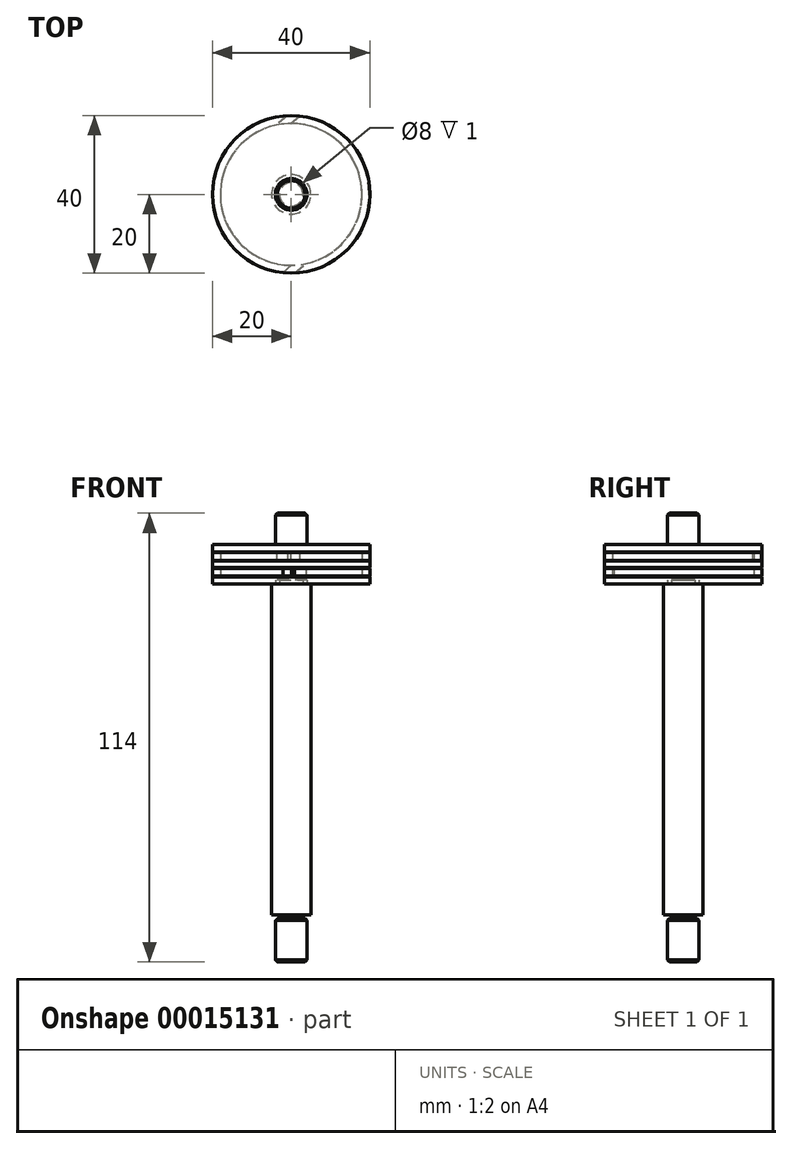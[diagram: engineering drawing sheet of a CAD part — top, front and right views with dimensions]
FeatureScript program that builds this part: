
annotation { "Feature Type Name" : "Feature", "Feature Type Description" : "" }
export const myFeature = defineFeature(function(context is Context, id is Id, definition is map)
    precondition{}
    {
        {
            var Q0;
            Q0=qCreatedBy(makeId("Front.planeOp"),FACE);
            var sketch = newSketch(context, id + "F0", { "sketchPlane" : qUnion([Q0])});
            skLineSegment(sketch, "E0", {"start": v(0, 0) * mm, "end": v(0, 13.15) * mm, "construction": true});
            skLineSegment(sketch, "E1", {"start": v(0, 0) * mm, "end": v(20, 0) * mm});
            skLineSegment(sketch, "E2", {"start": v(20, 0) * mm, "end": v(20, 2) * mm});
            skLineSegment(sketch, "E3", {"start": v(20, 2) * mm, "end": v(18, 2) * mm});
            skLineSegment(sketch, "E4", {"start": v(18, 2) * mm, "end": v(18, 4) * mm});
            skLineSegment(sketch, "E5", {"start": v(18, 4) * mm, "end": v(20, 4) * mm});
            skLineSegment(sketch, "E6", {"start": v(20, 4) * mm, "end": v(20, 6) * mm});
            skLineSegment(sketch, "E7", {"start": v(20, 6) * mm, "end": v(18, 6) * mm});
            skLineSegment(sketch, "E8", {"start": v(18, 6) * mm, "end": v(18, 8) * mm});
            skLineSegment(sketch, "E9", {"start": v(18, 8) * mm, "end": v(20, 8) * mm});
            skLineSegment(sketch, "E10", {"start": v(20, 8) * mm, "end": v(20, 10) * mm});
            skLineSegment(sketch, "E11", {"start": v(20, 10) * mm, "end": v(0, 10) * mm});
            skLineSegment(sketch, "E12", {"start": v(0, 10) * mm, "end": v(0, 0) * mm});
            skLineSegment(sketch, "E13", {"start": v(18, 10) * mm, "end": v(18, 0) * mm, "construction": true});
            skLineSegment(sketch, "E14", {"start": v(20, 10) * mm, "end": v(20, 0) * mm, "construction": true});
            skLineSegment(sketch, "E15.0.MirrorCS", {"start": v(-20, 10) * mm, "end": v(0, 10) * mm});
            skLineSegment(sketch, "E16.0.MirrorCS", {"start": v(0, 0) * mm, "end": v(-20, 0) * mm});
            skLineSegment(sketch, "E17.0.MirrorCS", {"start": v(-18, 2) * mm, "end": v(-18, 4) * mm});
            skLineSegment(sketch, "E18.0.MirrorCS", {"start": v(-18, 6) * mm, "end": v(-18, 8) * mm});
            skLineSegment(sketch, "E19.0.MirrorCS", {"start": v(-18, 8) * mm, "end": v(-20, 8) * mm});
            skLineSegment(sketch, "E20.0.MirrorCS", {"start": v(-20, 6) * mm, "end": v(-18, 6) * mm});
            skLineSegment(sketch, "E21.0.MirrorCS", {"start": v(-18, 4) * mm, "end": v(-20, 4) * mm});
            skLineSegment(sketch, "E22.0.MirrorCS", {"start": v(-20, 2) * mm, "end": v(-18, 2) * mm});
            skLineSegment(sketch, "E23.0.MirrorCS", {"start": v(-20, 0) * mm, "end": v(-20, 2) * mm});
            skLineSegment(sketch, "E24.0.MirrorCS", {"start": v(-20, 4) * mm, "end": v(-20, 6) * mm});
            skLineSegment(sketch, "E25.0.MirrorCS", {"start": v(-20, 8) * mm, "end": v(-20, 10) * mm});
            skLineSegment(sketch, "E26", {"start": v(4, 0) * mm, "end": v(4, 10) * mm});
            skLineSegment(sketch, "E27.0.MirrorCS", {"start": v(-4, 0) * mm, "end": v(-4, 10) * mm});
            skSolve(sketch);
        }
        {
            var Q0;
            {var subQ3=sQuery(id+"F0.wireOp",EDGE,"E2");Q0=makeQuery(id+"F0.imprint","IMPRINT",FACE,{"disambiguationData":[TD([[makeQuery(id+"F0.imprint","IMPRINT",EDGE,{"derivedFrom":subQ3}),1.0]])]});}
            var Q1;
            Q1=sQuery(id+"F0.wireOp",EDGE,"E0");
            revolve(context, id + "F1", {"entities" : qUnion([Q0]), "axis" : qUnion([Q1]), "revolveType" : RevolveType.FULL});
        }
        {
            var Q0;
            Q0=makeQuery(id+"F1.opRevolve","SWEPT_FACE",FACE,{"disambiguationData":[OSD([sQuery(id+"F0.wireOp",EDGE,"E3")])]});
            var sketch = newSketch(context, id + "F2", { "sketchPlane" : qUnion([Q0])});
            skArc(sketch, "E28.0", {"start": v(0.89, -19.98) * mm, "mid": v(0.63, 20) * mm, "end": v(-2.14, -19.89) * mm});
            skArc(sketch, "E29.0", {"start": v(3.75, -17.6) * mm, "mid": v(-1.96, 17.9) * mm, "end": v(0.14, -18) * mm});
            skLineSegment(sketch, "E30", {"start": v(0, 0) * mm, "end": v(0, -20) * mm, "construction": true});
            skLineSegment(sketch, "E31", {"start": v(0.14, -18) * mm, "end": v(-2.14, -19.89) * mm});
            skLineSegment(sketch, "E32", {"start": v(0.89, -19.98) * mm, "end": v(3.75, -17.6) * mm});
            skSolve(sketch);
        }
        {
            var Q0;
            Q0=makeQuery(id+"F2.imprint","IMPRINT",FACE,{"disambiguationData":[TD([[makeQuery(id+"F2.imprint","IMPRINT",EDGE,{"derivedFrom":sQuery(id+"F2.wireOp",EDGE,"E28.0")}),-1.0]])]});
            extrude(context, id + "F3", {"entities" : qUnion([Q0]), "depth" : 2 * mm});
        }
        {
            var Q0;
            Q0=makeQuery(id+"F1.opRevolve","SWEPT_EDGE",EDGE,{"disambiguationData":[OSD([sQuery(id+"F0.wireOp",EDGE,"E9"),sQuery(id+"F0.wireOp",EDGE,"E10")])]});
            var Q1;
            Q1=makeQuery(id+"F1.opRevolve","SWEPT_EDGE",EDGE,{"disambiguationData":[OSD([sQuery(id+"F0.wireOp",EDGE,"E6"),sQuery(id+"F0.wireOp",EDGE,"E7")])]});
            var Q2;
            Q2=makeQuery(id+"F1.opRevolve","SWEPT_EDGE",EDGE,{"disambiguationData":[OSD([sQuery(id+"F0.wireOp",EDGE,"E5"),sQuery(id+"F0.wireOp",EDGE,"E6")])]});
            var Q3;
            Q3=makeQuery(id+"F1.opRevolve","SWEPT_EDGE",EDGE,{"disambiguationData":[OSD([sQuery(id+"F0.wireOp",EDGE,"E2"),sQuery(id+"F0.wireOp",EDGE,"E3")])]});
            chamfer(context, id + "F4", {"entities" : qUnion([Q0, Q1, Q2, Q3]), "width" : .2 * mm, "tangentPropagation" : true});
        }
        {
            var Q0;
            Q0=makeQuery(id+"F3.opExtrude","SWEPT_BODY",BODY,{"disambiguationData":[OSD([sQuery(id+"F2.wireOp",EDGE,"E28.0"),sQuery(id+"F2.wireOp",EDGE,"E29.0"),sQuery(id+"F2.wireOp",EDGE,"E31"),sQuery(id+"F2.wireOp",EDGE,"E32")])]});
            var Q1;
            Q1=makeQuery(id+"F1.opRevolve","SWEPT_FACE",FACE,{"disambiguationData":[OSD([sQuery(id+"F0.wireOp",EDGE,"E26")])]});
            transform(context, id + "F5", {"entities" : qUnion([Q0]), "transformType" : TransformType.TRANSLATION_3D, "dx" : 0 * mm, "dy" : 0 * mm, "dz" : 4 * mm, "makeCopy" : true});
        }
        {
            var Q0;
            Q0=makeQuery(id+"F5.opPattern","COPY",BODY,{"derivedFrom":makeQuery(id+"F3.opExtrude","SWEPT_BODY",BODY,{"disambiguationData":[OSD([sQuery(id+"F2.wireOp",EDGE,"E28.0"),sQuery(id+"F2.wireOp",EDGE,"E29.0"),sQuery(id+"F2.wireOp",EDGE,"E31"),sQuery(id+"F2.wireOp",EDGE,"E32")])]}),"instanceName":"1"});
            var Q1;
            Q1=makeQuery(id+"F1.opRevolve","SWEPT_FACE",FACE,{"disambiguationData":[OSD([sQuery(id+"F0.wireOp",EDGE,"E26")])]});
            transform(context, id + "F6", {"entities" : qUnion([Q0]), "transformType" : TransformType.ROTATION, "transformAxis" : qUnion([Q1]), "angle" : 180 * degree, "makeCopy" : false});
        }
        {
            var Q0;
            Q0=makeQuery(id+"F1.opRevolve","SWEPT_FACE",FACE,{"disambiguationData":[OSD([sQuery(id+"F0.wireOp",EDGE,"E1")])]});
            var sketch = newSketch(context, id + "F7", { "sketchPlane" : qUnion([Q0])});
            skPoint(sketch, "E33.0", {"position": v(0, 0) * mm});
            skCircle(sketch, "E34", {"center": v(0, 0) * mm, "radius": 5 * mm});
            skCircle(sketch, "E35", {"center": v(0, 0) * mm, "radius": 3 * mm});
            skSolve(sketch);
        }
        {
            var Q0;
            Q0=makeQuery(id+"F7.imprint","IMPRINT",FACE,{"disambiguationData":[TD([[makeQuery(id+"F7.imprint","IMPRINT",EDGE,{"derivedFrom":sQuery(id+"F7.wireOp",EDGE,"E35")}),1.0]])]});
            var Q1;
            Q1=makeQuery(id+"F7.imprint","IMPRINT",FACE,{"disambiguationData":[TD([[makeQuery(id+"F7.imprint","IMPRINT",EDGE,{"derivedFrom":sQuery(id+"F7.wireOp",EDGE,"E35")}),-1.0]])]});
            var Q2;
            Q2=makeQuery(id+"F7.imprint","IMPRINT",FACE,{"disambiguationData":[TD([[makeQuery(id+"F7.imprint","IMPRINT",EDGE,{"derivedFrom":sQuery(id+"F7.wireOp",EDGE,"E34")}),1.0]])]});
            extrude(context, id + "F8", {"entities" : qUnion([Q0, Q1, Q2]), "depth" : (114 - 12 - 18) * mm});
        }
        {
            var Q0;
            Q0=makeQuery(id+"F7.imprint","IMPRINT",FACE,{"disambiguationData":[TD([[makeQuery(id+"F7.imprint","IMPRINT",EDGE,{"derivedFrom":sQuery(id+"F7.wireOp",EDGE,"E35")}),1.0]])]});
            extrude(context, id + "F9", {"entities" : qUnion([Q0]), "operationType" : NewBodyOperationType.ADD, "oppositeDirection" : true, "depth" : 1 * mm});
        }
        {
            var Q0;
            Q0=makeQuery(id+"F9.opExtrude","CAP_FACE",FACE,{"disambiguationData":[OSD([sQuery(id+"F7.wireOp",EDGE,"E35")])],"isStart":false});
            var sketch = newSketch(context, id + "F10", { "sketchPlane" : qUnion([Q0])});
            skCircle(sketch, "E36.0.0", {"center": v(0, 0) * mm, "radius": 5 * mm, "construction": true});
            skCircle(sketch, "E37.0.0", {"center": v(0, 0) * mm, "radius": 5 * mm});
            skCircle(sketch, "E38", {"center": v(0, 0) * mm, "radius": 4 * mm});
            skSolve(sketch);
        }
        {
            var Q0;
            Q0=makeQuery(id+"F10.imprint","IMPRINT",FACE,{"disambiguationData":[TD([[makeQuery(id+"F10.imprint","IMPRINT",EDGE,{"derivedFrom":makeQuery(id+"F9.opExtrude","CAP_EDGE",EDGE,{"disambiguationData":[OSD([sQuery(id+"F7.wireOp",EDGE,"E35")])],"isStart":false})}),-1.0]])]});
            var Q1;
            Q1=makeQuery(id+"F10.imprint","IMPRINT",FACE,{"disambiguationData":[TD([[makeQuery(id+"F10.imprint","IMPRINT",EDGE,{"derivedFrom":sQuery(id+"F10.wireOp",EDGE,"E38")}),1.0]])]});
            extrude(context, id + "F11", {"entities" : qUnion([Q0, Q1]), "operationType" : NewBodyOperationType.ADD, "depth" : (18 - 1) * mm});
        }
        {
            var Q0;
            Q0=makeQuery(id+"F8.opExtrude","CAP_FACE",FACE,{"disambiguationData":[OSD([sQuery(id+"F7.wireOp",EDGE,"E34")])],"isStart":false});
            var sketch = newSketch(context, id + "F12", { "sketchPlane" : qUnion([Q0])});
            skCircle(sketch, "E39.0.0", {"center": v(0, 0) * mm, "radius": 5 * mm});
            skCircle(sketch, "E40", {"center": v(0, 0) * mm, "radius": 3 * mm});
            skSolve(sketch);
        }
        {
            var Q0;
            Q0=makeQuery(id+"F12.imprint","IMPRINT",FACE,{"disambiguationData":[TD([[makeQuery(id+"F12.imprint","IMPRINT",EDGE,{"derivedFrom":sQuery(id+"F12.wireOp",EDGE,"E40")}),1.0]])]});
            extrude(context, id + "F13", {"entities" : qUnion([Q0]), "operationType" : NewBodyOperationType.ADD, "depth" : 1 * mm});
        }
        {
            var Q0;
            Q0=makeQuery(id+"F13.opExtrude","CAP_FACE",FACE,{"disambiguationData":[OSD([sQuery(id+"F12.wireOp",EDGE,"E40")])],"isStart":false});
            var sketch = newSketch(context, id + "F14", { "sketchPlane" : qUnion([Q0])});
            skCircle(sketch, "E41.0.0", {"center": v(0, 0) * mm, "radius": 3 * mm});
            skCircle(sketch, "E42", {"center": v(0, 0) * mm, "radius": 4 * mm});
            skSolve(sketch);
        }
        {
            var Q0;
            Q0=makeQuery(id+"F14.imprint","IMPRINT",FACE,{"disambiguationData":[TD([[makeQuery(id+"F14.imprint","IMPRINT",EDGE,{"derivedFrom":sQuery(id+"F14.wireOp",EDGE,"E41.0.0")}),1.0]])]});
            var Q1;
            Q1=makeQuery(id+"F14.imprint","IMPRINT",FACE,{"disambiguationData":[TD([[makeQuery(id+"F14.imprint","IMPRINT",EDGE,{"derivedFrom":sQuery(id+"F14.wireOp",EDGE,"E41.0.0")}),-1.0]])]});
            extrude(context, id + "F15", {"entities" : qUnion([Q0, Q1]), "operationType" : NewBodyOperationType.ADD, "depth" : (12 - 1) * mm});
        }
        {
            var Q0;
            Q0=makeQuery(id+"F15.opExtrude","CAP_EDGE",EDGE,{"disambiguationData":[OSD([sQuery(id+"F14.wireOp",EDGE,"E42")])],"isStart":false});
            var Q1;
            Q1=makeQuery(id+"F11.opExtrude","CAP_EDGE",EDGE,{"disambiguationData":[OSD([sQuery(id+"F10.wireOp",EDGE,"E38")])],"isStart":false});
            var Q2;
            Q2=makeQuery(id+"F15.opExtrude","CAP_EDGE",EDGE,{"disambiguationData":[OSD([sQuery(id+"F14.wireOp",EDGE,"E42")])],"isStart":true});
            var Q3;
            Q3=makeQuery(id+"F11.opExtrude","CAP_EDGE",EDGE,{"disambiguationData":[OSD([sQuery(id+"F10.wireOp",EDGE,"E38")])],"isStart":true});
            chamfer(context, id + "F16", {"entities" : qUnion([Q0, Q1, Q2, Q3]), "width" : .5 * mm, "tangentPropagation" : true});
        }
    });
